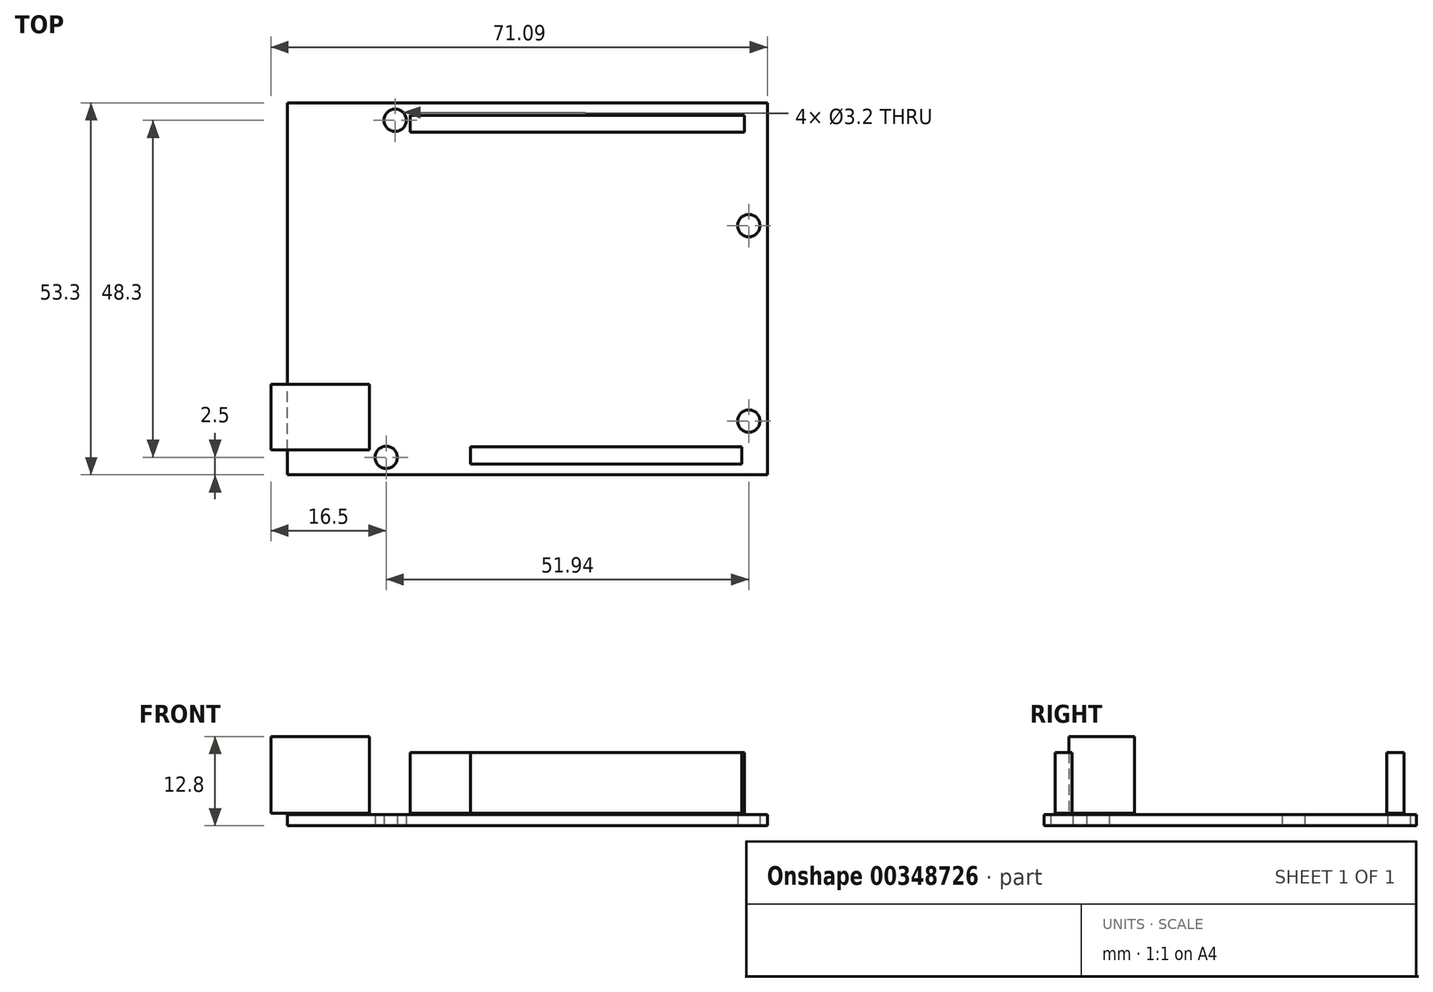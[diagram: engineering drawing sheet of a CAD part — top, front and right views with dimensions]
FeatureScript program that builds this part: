
annotation { "Feature Type Name" : "Feature", "Feature Type Description" : "" }
export const myFeature = defineFeature(function(context is Context, id is Id, definition is map)
    precondition{}
    {
        {
            var Q0;
            Q0=qCreatedBy(makeId("Top.planeOp"),FACE);
            var sketch = newSketch(context, id + "F0", { "sketchPlane" : qUnion([Q0])});
            skLineSegment(sketch, "E0", {"start": v(0, 0) * mm, "end": v(0, 53.3) * mm});
            skLineSegment(sketch, "E1", {"start": v(-1.66, 26.65) * mm, "end": v(71.96, 26.65) * mm, "construction": true});
            skCircle(sketch, "E2", {"center": v(14.16, 2.5) * mm, "radius": 1.6 * mm});
            skLineSegment(sketch, "E3", {"start": v(68.75, 53.3) * mm, "end": v(68.75, 0) * mm});
            skCircle(sketch, "E4", {"center": v(15.45, 50.8) * mm, "radius": 1.6 * mm});
            skCircle(sketch, "E5", {"center": v(66.1, 7.7) * mm, "radius": 1.6 * mm});
            skCircle(sketch, "E6", {"center": v(66.1, 35.7) * mm, "radius": 1.6 * mm});
            skLineSegment(sketch, "E7", {"start": v(0, 0) * mm, "end": v(68.75, 0) * mm});
            skLineSegment(sketch, "E8.MirrorCS", {"start": v(0, 53.3) * mm, "end": v(68.75, 53.3) * mm});
            skSolve(sketch);
        }
        {
            var Q0;
            Q0=makeQuery(id+"F0.imprint","IMPRINT",FACE,{"disambiguationData":[TD([[makeQuery(id+"F0.imprint","IMPRINT",EDGE,{"derivedFrom":sQuery(id+"F0.wireOp",EDGE,"E0")}),-1.0]])]});
            extrude(context, id + "F1", {"entities" : qUnion([Q0]), "depth" : 1.6 * mm});
        }
        {
            var Q0;
            Q0=makeQuery(id+"F1.opExtrude","CAP_FACE",FACE,{"disambiguationData":[OSD([sQuery(id+"F0.wireOp",EDGE,"E0"),sQuery(id+"F0.wireOp",EDGE,"E2"),sQuery(id+"F0.wireOp",EDGE,"E3"),sQuery(id+"F0.wireOp",EDGE,"E4"),sQuery(id+"F0.wireOp",EDGE,"E5"),sQuery(id+"F0.wireOp",EDGE,"E6"),sQuery(id+"F0.wireOp",EDGE,"E7"),sQuery(id+"F0.wireOp",EDGE,"E8.MirrorCS")])],"isStart":false});
            cPlane(context, id + "F2", {"entities" : qUnion([Q0]), "cplaneType" : CPlaneType.OFFSET, "offset" : 0.2 * mm, "width" : 150 * mm, "height" : 150 * mm});
        }
        {
            var Q0;
            Q0=qCreatedBy(id+"F2.planeOp",FACE);
            var sketch = newSketch(context, id + "F3", { "sketchPlane" : qUnion([Q0])});
            skLineSegment(sketch, "E9.bottom", {"start": v(11.78, 12.95) * mm, "end": v(-2.34, 12.95) * mm});
            skLineSegment(sketch, "E9.top", {"start": v(11.78, 3.55) * mm, "end": v(-2.34, 3.55) * mm});
            skLineSegment(sketch, "E9.left", {"start": v(11.78, 12.95) * mm, "end": v(11.78, 3.55) * mm});
            skLineSegment(sketch, "E9.right", {"start": v(-2.34, 12.95) * mm, "end": v(-2.34, 3.55) * mm});
            skLineSegment(sketch, "E10.bottom", {"start": v(26.26, 4) * mm, "end": v(65.07, 4) * mm});
            skLineSegment(sketch, "E10.top", {"start": v(26.26, 1.55) * mm, "end": v(65.07, 1.55) * mm});
            skLineSegment(sketch, "E10.left", {"start": v(26.26, 4) * mm, "end": v(26.26, 1.55) * mm});
            skLineSegment(sketch, "E10.right", {"start": v(65.07, 4) * mm, "end": v(65.07, 1.55) * mm});
            skLineSegment(sketch, "E11.bottom", {"start": v(17.6, 51.54) * mm, "end": v(65.5, 51.54) * mm});
            skLineSegment(sketch, "E11.top", {"start": v(17.6, 49.1) * mm, "end": v(65.5, 49.1) * mm});
            skLineSegment(sketch, "E11.left", {"start": v(17.6, 51.54) * mm, "end": v(17.6, 49.1) * mm});
            skLineSegment(sketch, "E11.right", {"start": v(65.5, 51.54) * mm, "end": v(65.5, 49.1) * mm});
            skSolve(sketch);
        }
        {
            var Q0;
            Q0=makeQuery(id+"F3.imprint","IMPRINT",FACE,{"disambiguationData":[TD([[makeQuery(id+"F3.imprint","IMPRINT",EDGE,{"derivedFrom":sQuery(id+"F3.wireOp",EDGE,"E9.bottom")}),1.0]])]});
            extrude(context, id + "F4", {"entities" : qUnion([Q0]), "depth" : 11 * mm});
        }
        {
            var Q0;
            Q0=makeQuery(id+"F3.imprint","IMPRINT",FACE,{"disambiguationData":[TD([[makeQuery(id+"F3.imprint","IMPRINT",EDGE,{"derivedFrom":sQuery(id+"F3.wireOp",EDGE,"E11.bottom")}),-1.0]])]});
            var Q1;
            Q1=makeQuery(id+"F3.imprint","IMPRINT",FACE,{"disambiguationData":[TD([[makeQuery(id+"F3.imprint","IMPRINT",EDGE,{"derivedFrom":sQuery(id+"F3.wireOp",EDGE,"E10.bottom")}),-1.0]])]});
            extrude(context, id + "F5", {"entities" : qUnion([Q0, Q1]), "depth" : 8.7 * mm});
        }
    });
